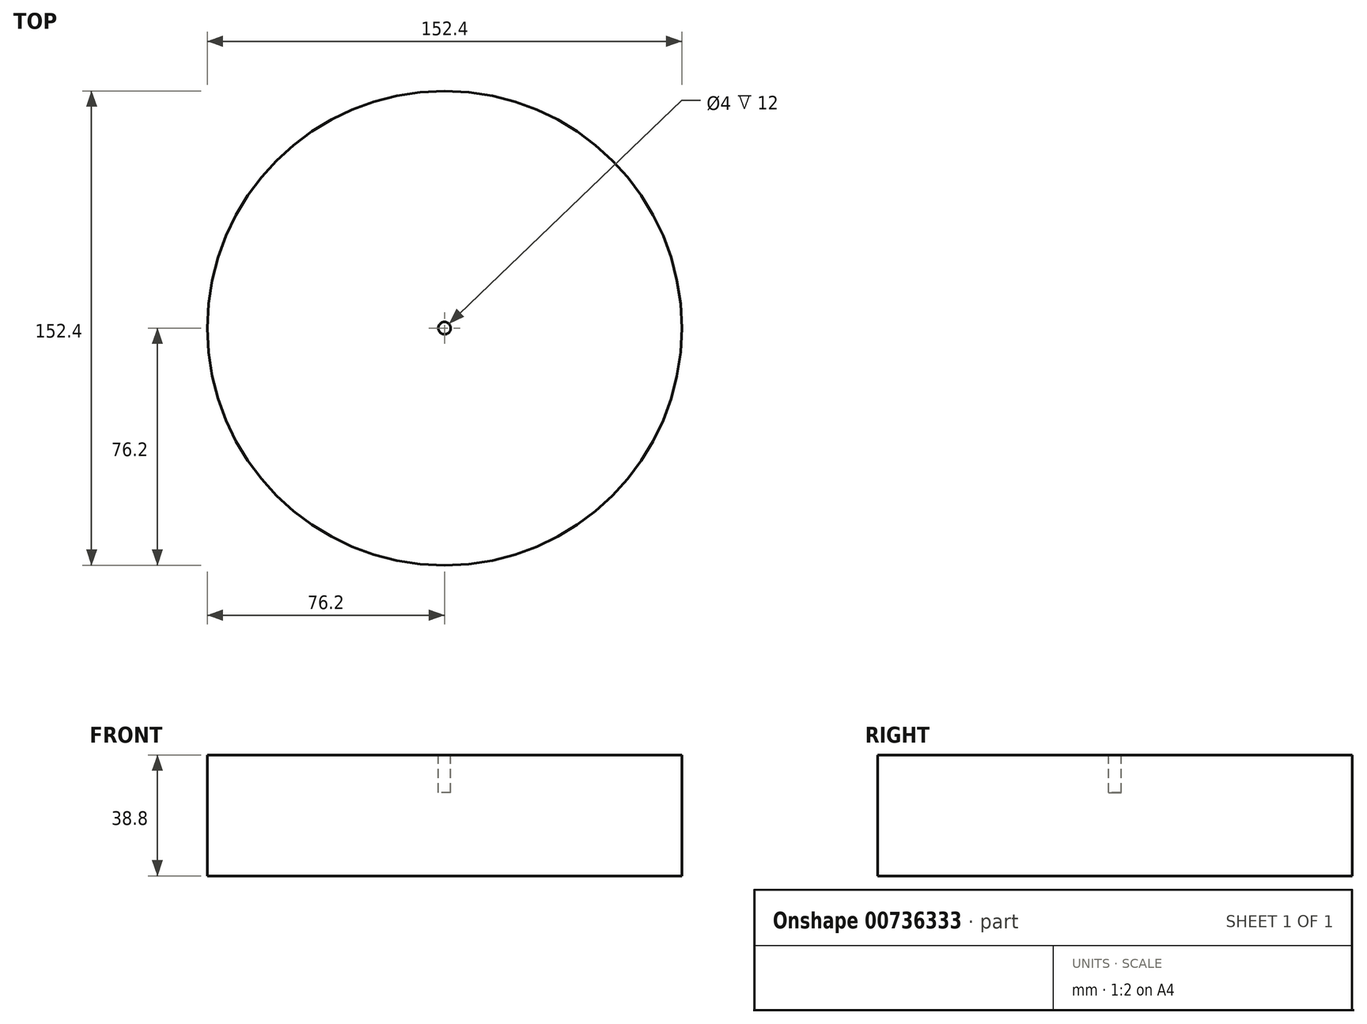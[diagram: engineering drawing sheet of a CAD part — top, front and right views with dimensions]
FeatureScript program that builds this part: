
annotation { "Feature Type Name" : "Feature", "Feature Type Description" : "" }
export const myFeature = defineFeature(function(context is Context, id is Id, definition is map)
    precondition{}
    {
        {
            var Q0;
            Q0=qCreatedBy(makeId("Top.planeOp"),FACE);
            var sketch = newSketch(context, id + "F0", { "sketchPlane" : qUnion([Q0])});
            skCircle(sketch, "E0", {"center": v(0.04, -0.03) * mm, "radius": 2 * mm});
            skCircle(sketch, "E1", {"center": v(0.04, -0.03) * mm, "radius": 9 * mm});
            skSolve(sketch);
        }
        {
            var Q0;
            Q0 = qSketchRegion(id + "F0", true);
            extrude(context, id + "F1", {"entities" : qUnion([Q0]), "oppositeDirection" : true, "depth" : 12 * mm, "offsetDistance" : 25 * mm});
        }
        {
            var Q0;
            Q0=qCreatedBy(makeId("Top.planeOp"),FACE);
            var sketch = newSketch(context, id + "F2", { "sketchPlane" : qUnion([Q0])});
            skCircle(sketch, "E2", {"center": v(0, 0) * mm, "radius": 76.2 * mm});
            skSolve(sketch);
        }
        {
            var Q0;
            Q0 = qSketchRegion(id + "F2", true);
            extrude(context, id + "F3", {"entities" : qUnion([Q0]), "operationType" : NewBodyOperationType.ADD, "oppositeDirection" : true, "depth" : 38.8 * mm, "offsetDistance" : 25 * mm});
        }
        {
            var Q0;
            Q0=makeQuery(id+"F3.boolean.opBoolean","SPLIT",FACE,{"disambiguationData":[TD([makeQuery(id+"F1.opExtrude","SWEPT_FACE",FACE,{"disambiguationData":[OSD([sQuery(id+"F0.wireOp",EDGE,"E0")])]})])],"derivedFrom":makeQuery(id+"F3.opExtrude","CAP_FACE",FACE,{"disambiguationData":[OSD([sQuery(id+"F2.wireOp",EDGE,"E2")])],"isStart":true})});
            var sketch = newSketch(context, id + "F4", { "sketchPlane" : qUnion([Q0])});
            skSolve(sketch);
        }
        {
            var Q0;
            Q0=makeQuery(id+"F4.imprint","IMPRINT",FACE,{"disambiguationData":[TD([[makeQuery(id+"F4.imprint","IMPRINT",EDGE,{"derivedFrom":makeQuery(id+"F3.opExtrude","CAP_EDGE",EDGE,{"disambiguationData":[OSD([sQuery(id+"F2.wireOp",EDGE,"E2")])],"isStart":true})}),1.0]])]});
            var sketch = newSketch(context, id + "F5", { "sketchPlane" : qUnion([Q0])});
            skCircle(sketch, "E3", {"center": v(0, 0) * mm, "radius": 2 * mm});
            skSolve(sketch);
        }
        {
            var Q0;
            Q0 = qSketchRegion(id + "F5", true);
            extrude(context, id + "F6", {"entities" : qUnion([Q0]), "operationType" : NewBodyOperationType.REMOVE, "oppositeDirection" : true, "depth" : 12 * mm, "offsetDistance" : 25 * mm});
        }
    });
